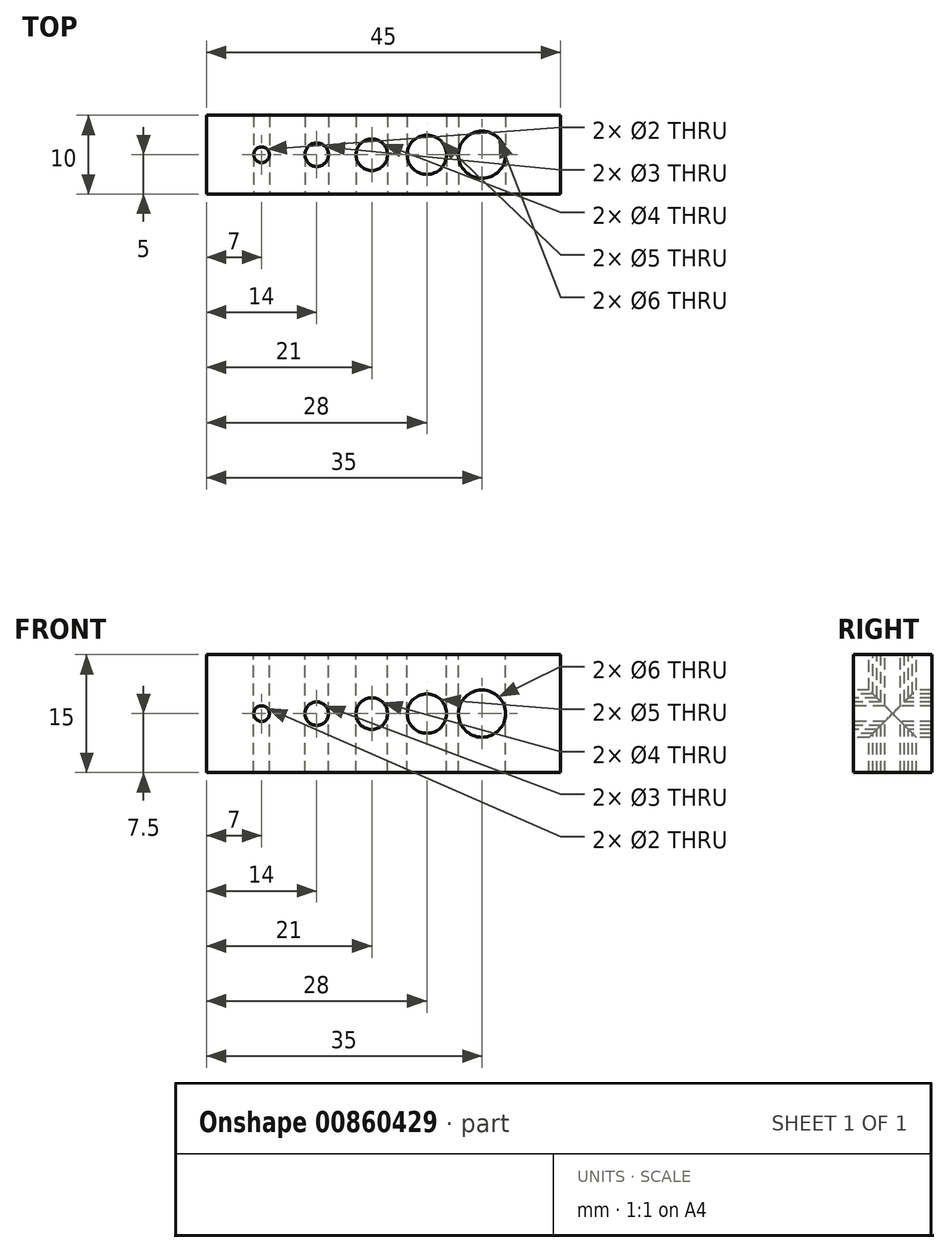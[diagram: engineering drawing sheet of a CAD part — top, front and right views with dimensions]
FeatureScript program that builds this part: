
annotation { "Feature Type Name" : "Feature", "Feature Type Description" : "" }
export const myFeature = defineFeature(function(context is Context, id is Id, definition is map)
    precondition{}
    {
        {
            var Q0;
            Q0=qCreatedBy(makeId("Top.planeOp"),FACE);
            var sketch = newSketch(context, id + "F0", { "sketchPlane" : qUnion([Q0])});
            skLineSegment(sketch, "E0.bottom", {"start": v(22.5, -5) * mm, "end": v(-22.5, -5) * mm});
            skLineSegment(sketch, "E0.top", {"start": v(22.5, 5) * mm, "end": v(-22.5, 5) * mm});
            skLineSegment(sketch, "E0.left", {"start": v(22.5, -5) * mm, "end": v(22.5, 5) * mm});
            skLineSegment(sketch, "E0.right", {"start": v(-22.5, -5) * mm, "end": v(-22.5, 5) * mm});
            skPoint(sketch, "E0.middle", {"position": v(0, 0) * mm});
            skSolve(sketch);
        }
        {
            var Q0;
            Q0 = qSketchRegion(id + "F0", true);
            extrude(context, id + "F1", {"entities" : qUnion([Q0]), "depth" : 15 * mm, "offsetDistance" : 25 * mm});
        }
        {
            var Q0;
            Q0=makeQuery(id+"F1.opExtrude","SWEPT_FACE",FACE,{"disambiguationData":[OSD([sQuery(id+"F0.wireOp",EDGE,"E0.bottom")])]});
            var sketch = newSketch(context, id + "F2", { "sketchPlane" : qUnion([Q0])});
            skCircle(sketch, "E1", {"center": v(-15.5, 7.5) * mm, "radius": 1 * mm});
            skCircle(sketch, "E2", {"center": v(-8.5, 7.5) * mm, "radius": 1.5 * mm});
            skCircle(sketch, "E3", {"center": v(-1.5, 7.5) * mm, "radius": 2 * mm});
            skCircle(sketch, "E4", {"center": v(5.5, 7.5) * mm, "radius": 2.5 * mm});
            skCircle(sketch, "E5", {"center": v(12.5, 7.5) * mm, "radius": 3 * mm});
            skSolve(sketch);
        }
        {
            var Q0;
            Q0 = qSketchRegion(id + "F2", true);
            var Q1;
            Q1=makeQuery(id+"F1.opExtrude","SWEPT_FACE",FACE,{"disambiguationData":[OSD([sQuery(id+"F0.wireOp",EDGE,"E0.top")])]});
            extrude(context, id + "F3", {"entities" : qUnion([Q0]), "operationType" : NewBodyOperationType.REMOVE, "endBound" : BoundingType.UP_TO_SURFACE, "oppositeDirection" : true, "depth" : 25 * mm, "endBoundEntityFace" : qUnion([Q1]), "offsetDistance" : 25 * mm});
        }
        {
            var Q0;
            Q0=makeQuery(id+"F1.opExtrude","CAP_FACE",FACE,{"disambiguationData":[OSD([sQuery(id+"F0.wireOp",EDGE,"E0.bottom"),sQuery(id+"F0.wireOp",EDGE,"E0.top"),sQuery(id+"F0.wireOp",EDGE,"E0.left"),sQuery(id+"F0.wireOp",EDGE,"E0.right")])],"isStart":false});
            var sketch = newSketch(context, id + "F4", { "sketchPlane" : qUnion([Q0])});
            skLineSegment(sketch, "E6.0", {"start": v(-14.5, -5) * mm, "end": v(-16.5, -5) * mm, "construction": true});
            skLineSegment(sketch, "E7.0", {"start": v(-7, -5) * mm, "end": v(-10, -5) * mm, "construction": true});
            skLineSegment(sketch, "E8.0", {"start": v(0.5, -5) * mm, "end": v(-3.5, -5) * mm, "construction": true});
            skLineSegment(sketch, "E9.0", {"start": v(8, -5) * mm, "end": v(3, -5) * mm, "construction": true});
            skLineSegment(sketch, "E10.0", {"start": v(15.5, -5) * mm, "end": v(9.5, -5) * mm, "construction": true});
            skCircle(sketch, "E11", {"center": v(-15.5, 0) * mm, "radius": 1 * mm});
            skPoint(sketch, "E11.centerSnap0", {"position": v(-15.5, -5) * mm});
            skCircle(sketch, "E12", {"center": v(-8.5, 0) * mm, "radius": 1.5 * mm});
            skPoint(sketch, "E12.centerSnap0", {"position": v(-8.5, -5) * mm});
            skCircle(sketch, "E13", {"center": v(-1.5, 0) * mm, "radius": 2 * mm});
            skPoint(sketch, "E13.centerSnap0", {"position": v(-1.5, -5) * mm});
            skCircle(sketch, "E14", {"center": v(5.5, 0) * mm, "radius": 2.5 * mm});
            skPoint(sketch, "E14.centerSnap0", {"position": v(5.5, -5) * mm});
            skCircle(sketch, "E15", {"center": v(12.5, 0) * mm, "radius": 3 * mm});
            skPoint(sketch, "E15.centerSnap0", {"position": v(12.5, -5) * mm});
            skSolve(sketch);
        }
        {
            var Q0;
            Q0 = qSketchRegion(id + "F4", true);
            var Q1;
            Q1=makeQuery(id+"F1.opExtrude","CAP_FACE",FACE,{"disambiguationData":[OSD([sQuery(id+"F0.wireOp",EDGE,"E0.bottom"),sQuery(id+"F0.wireOp",EDGE,"E0.top"),sQuery(id+"F0.wireOp",EDGE,"E0.left"),sQuery(id+"F0.wireOp",EDGE,"E0.right")])],"isStart":true});
            extrude(context, id + "F5", {"entities" : qUnion([Q0]), "operationType" : NewBodyOperationType.REMOVE, "endBound" : BoundingType.UP_TO_SURFACE, "oppositeDirection" : true, "depth" : 25 * mm, "endBoundEntityFace" : qUnion([Q1]), "offsetDistance" : 25 * mm});
        }
    });
